# Revit family: xxxWash_Fountain-Three_Station-Acorn_Engineering-3493_Series
name_source: partatom
category: Plumbing Fixtures
units: mm (PartAtom-declared; Revit-internal decimal feet)

## family parameters
Cut with Voids When Loaded = Yes
Host = Face
OmniClass Number = 23.65.70.14.11
OmniClass Title = Drinking Fountains/Coolers
Part Type = Normal
Room Calculation Point = No
Round Connector Dimension = Use Diameter
Shared = Yes

## types (2) — shared parameters
-EG Enviro-Glaze Powder Coat = No
-H Hand Operation = No
-H120 Tankless Water Heater, 20 amp 120 volt = No
-H240 Tankless Water Heater, 20 amp 240 volt = No
-LID Stainless Steel Sprayhead Lid = No
-SO Sensor Operation = No
-SO-BAT Sensor Operation (Batteries Not Included) = No
-SSO Sensor Soap (32oz Liquid Soap) = Yes
-SSO-BAT Sensor Soap Operation, Battery Powered = No
-ST Single Temperature Valve = No
36” Solid Surface Semi-Circular, Three Station = No
ASME A112.18.1/CSA B125.1 = Yes
Activation = Hands-free Sensor
Assembly Code = D2010800
Basin Length = 23"
Bowl Depth = 7 3/4"
CW Connection = Yes
CWFU = 1.5
Cold Water Connection Diameter = 1/2"
Cold Water Connection Height = 13 1/2"
Default Elevation = 0"
Description = Three Station, 7-3/4" Deep Bowl, Semi-Circular Wash Fountain - ADA Compliant
Drain Offset = 5 1/8"
Finish = Polymer Resin-Acorn-Corterra-OCC11M Blanco-Matte
Finish - Sensor = Black
Finish- Grid Strainer = Metal-Acorn-Stainless Steel-Chrome Plated
Finish- Others = Metal-Acorn-Stainless Steel
Finish- Trap Enclosure = Stainless Steel-Acorn-Type 304-16 Gauge-Satin
Flow Rate = 0.35 GPM (1.59 LPM)
HW Connection = No
HWFU = 1.5
Hot Water Connection Diameter = 1/2"
Hot Water Connection Height = 13 1/2"
Installation Instruction Link = https://www.acorneng.com
Installation Type = Wall Mounted
Manufacturer = Acorn Engineering
Material = Polymer Resin-Acorn-Corterra-OCC11M Blanco-Matte
NSF/ANSI 372 = Yes
Pressure Range = 30 PSI
Price = Prices may vary. Please consult Manufacturer Representative for most up-to-date price list.
Product Documentation Link = https://www.acorneng.com
Product Page URL = https://www.acorneng.com
Soap Bottle Capacity = Large 32 oz. (0.95 L)
URL = https://www.acorneng.com
Vent Connection = No
WFU = 2
Warranty Information = 1 Year Limited Warranty
Waste Connection = Yes
Waste Connection Diameter = 1 1/2"
Waste Connection Height = 20 3/4"
Waste Connection Offset (from C/L) = 1 1/2"
Width = 36"
cUPC Compliant = Yes

## per-type parameters (varying)
| type | -OBC Trap Cover for OBC (Canadian) Compliance | ADA Compliant | ADA Profile | California Building Code (CBC) Compliant | OBC Profile | Ontario Building Code (OBC) Compliant | Trap Enclosure |
| 3493-ADA | No | Yes | Yes | Yes | No | No | 5 3/8" |
| 3493-OBC | Yes | No | No | No | Yes | Yes | 5 3/4" |

note: column(s) folded — value = type name in every type: Model

## geometry (parser evidence)
native form markers: Sweep x2
no freeform markers — native parametric forms only
